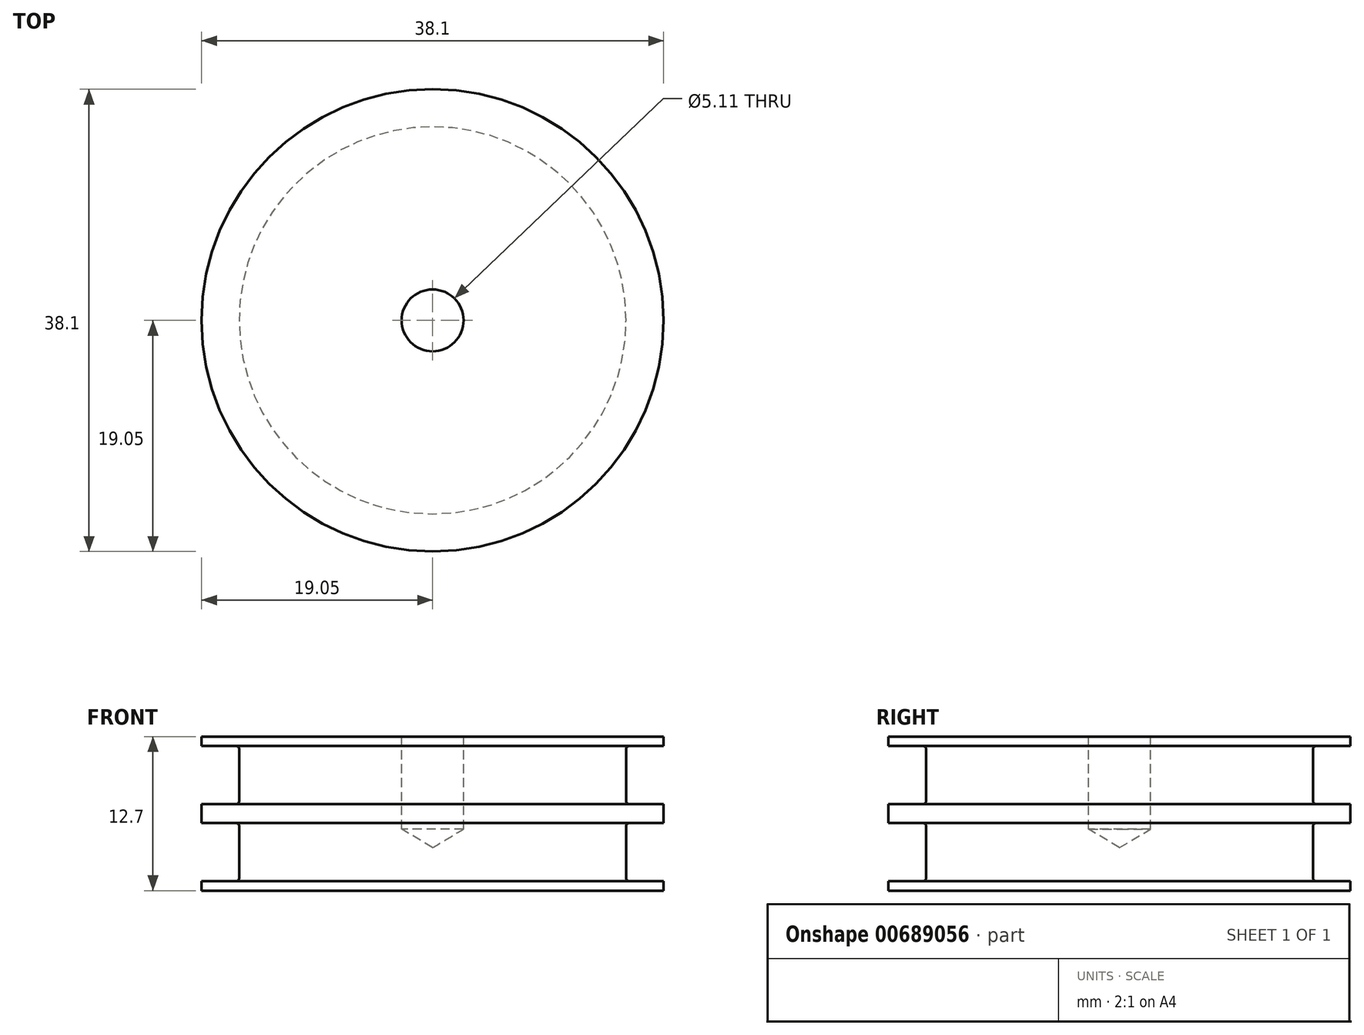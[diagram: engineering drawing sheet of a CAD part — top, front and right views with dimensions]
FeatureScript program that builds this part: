
annotation { "Feature Type Name" : "Feature", "Feature Type Description" : "" }
export const myFeature = defineFeature(function(context is Context, id is Id, definition is map)
    precondition{}
    {
        {
            var Q0;
            Q0=qCreatedBy(makeId("Front.planeOp"),FACE);
            var sketch = newSketch(context, id + "F0", { "sketchPlane" : qUnion([Q0])});
            skLineSegment(sketch, "E0.bottom", {"start": v(0, 12.7) * mm, "end": v(19.05, 12.7) * mm});
            skLineSegment(sketch, "E0.top", {"start": v(0, 0) * mm, "end": v(19.05, 0) * mm});
            skLineSegment(sketch, "E0.left", {"start": v(0, 12.7) * mm, "end": v(0, 0) * mm});
            skLineSegment(sketch, "E0.right", {"start": v(19.05, 12.7) * mm, "end": v(19.05, 11.91) * mm});
            skPoint(sketch, "E1", {"position": v(19.05, 6.35) * mm});
            skLineSegment(sketch, "E2", {"start": v(19.05, 6.35) * mm, "end": v(-2.1, 6.35) * mm, "construction": true});
            skPoint(sketch, "E3", {"position": v(19.05, 3.18) * mm});
            skLineSegment(sketch, "E4.top", {"start": v(19.05, 5.56) * mm, "end": v(16.2, 5.56) * mm});
            skLineSegment(sketch, "E4.right", {"start": v(15.95, 3.17) * mm, "end": v(15.95, 5.3) * mm});
            skLineSegment(sketch, "E5", {"start": v(15.95, 3.18) * mm, "end": v(3.84, 3.17) * mm, "construction": true});
            skLineSegment(sketch, "E6.MirrorCS", {"start": v(19.05, 0.79) * mm, "end": v(16.2, 0.79) * mm});
            skLineSegment(sketch, "E7.MirrorCS", {"start": v(15.95, 3.17) * mm, "end": v(15.95, 1.04) * mm});
            skPoint(sketch, "E8.visualSharp", {"position": v(15.95, 5.56) * mm});
            skArc(sketch, "E8.filletArc", {"start": v(16.2, 5.56) * mm, "mid": v(16.03, 5.49) * mm, "end": v(15.95, 5.3) * mm});
            skPoint(sketch, "E9.visualSharp", {"position": v(15.95, 0.79) * mm});
            skArc(sketch, "E9.filletArc", {"start": v(15.95, 1.04) * mm, "mid": v(16.03, 0.86) * mm, "end": v(16.2, 0.79) * mm});
            skLineSegment(sketch, "E10.MirrorCS", {"start": v(19.05, 7.14) * mm, "end": v(16.2, 7.14) * mm});
            skLineSegment(sketch, "E11.MirrorCS", {"start": v(15.95, 9.53) * mm, "end": v(15.95, 7.4) * mm});
            skLineSegment(sketch, "E12.MirrorCS", {"start": v(15.95, 9.53) * mm, "end": v(15.95, 11.66) * mm});
            skLineSegment(sketch, "E13.MirrorCS", {"start": v(19.05, 11.91) * mm, "end": v(16.2, 11.91) * mm});
            skLineSegment(sketch, "E14.trimOffspring", {"start": v(19.05, 7.14) * mm, "end": v(19.05, 5.56) * mm});
            skArc(sketch, "E15.MirrorCS", {"start": v(16.2, 7.14) * mm, "mid": v(16.03, 7.21) * mm, "end": v(15.95, 7.4) * mm});
            skArc(sketch, "E16.MirrorCS", {"start": v(15.95, 11.66) * mm, "mid": v(16.03, 11.84) * mm, "end": v(16.2, 11.91) * mm});
            skLineSegment(sketch, "E17.trimOffspring", {"start": v(19.05, 0.79) * mm, "end": v(19.05, 0) * mm});
            skSolve(sketch);
        }
        {
            var Q0;
            Q0=makeQuery(id+"F0.imprint","IMPRINT",FACE,{"disambiguationData":[TD([[makeQuery(id+"F0.imprint","IMPRINT",EDGE,{"derivedFrom":sQuery(id+"F0.wireOp",EDGE,"E0.bottom")}),-1.0]])]});
            var Q1;
            Q1=sQuery(id+"F0.wireOp",EDGE,"E0.left");
            revolve(context, id + "F1", {"entities" : qUnion([Q0]), "axis" : qUnion([Q1]), "revolveType" : RevolveType.FULL});
        }
        {
            var Q0;
            Q0=makeQuery(id+"F1.opRevolve","SWEPT_FACE",FACE,{"disambiguationData":[OSD([sQuery(id+"F0.wireOp",EDGE,"E0.bottom")])]});
            var sketch = newSketch(context, id + "F2", { "sketchPlane" : qUnion([Q0])});
            skPoint(sketch, "E18", {"position": v(0, 0) * mm});
            skSolve(sketch);
        }
        {
            var Q0;
            Q0=sQuery(id+"F2.wireOp",VERTEX,"E18");
            var Q1;
            Q1=makeQuery(id+"F1.opRevolve","SWEPT_BODY",BODY,{"disambiguationData":[OSD([sQuery(id+"F0.wireOp",EDGE,"E0.bottom"),sQuery(id+"F0.wireOp",EDGE,"E0.top"),sQuery(id+"F0.wireOp",EDGE,"E0.left"),sQuery(id+"F0.wireOp",EDGE,"E0.right"),sQuery(id+"F0.wireOp",EDGE,"E4.top"),sQuery(id+"F0.wireOp",EDGE,"E4.right"),sQuery(id+"F0.wireOp",EDGE,"E6.MirrorCS"),sQuery(id+"F0.wireOp",EDGE,"E7.MirrorCS"),sQuery(id+"F0.wireOp",EDGE,"E8.filletArc"),sQuery(id+"F0.wireOp",EDGE,"E9.filletArc"),sQuery(id+"F0.wireOp",EDGE,"E10.MirrorCS"),sQuery(id+"F0.wireOp",EDGE,"E11.MirrorCS"),sQuery(id+"F0.wireOp",EDGE,"E12.MirrorCS"),sQuery(id+"F0.wireOp",EDGE,"E13.MirrorCS"),sQuery(id+"F0.wireOp",EDGE,"E14.trimOffspring"),sQuery(id+"F0.wireOp",EDGE,"E15.MirrorCS"),sQuery(id+"F0.wireOp",EDGE,"E16.MirrorCS"),sQuery(id+"F0.wireOp",EDGE,"E17.trimOffspring")])]});
            hole(context, id + "F3", {"style" : HoleStyle.SIMPLE, "endStyle" : HoleEndStyle.BLIND, "standardTappedOrClearance" : lookupTablePath({ "standard" : "ANSI", "engagement" : "75%", "pitch" : "20 tpi", "size" : "1/4", "type" : "Tapped" }), "standardBlindInLast" : lookupTablePath({ "standard" : "ANSI", "engagement" : "75%", "pitch" : "20 tpi", "size" : "1/4", "type" : "Tapped" }), "holeDiameter" : 5.1 * mm, "majorDiameter" : 6.35 * mm, "showTappedDepth" : true, "holeDepth" : 7.62 * mm, "isTappedThrough" : true, "tappedDepth" : 6.35 * mm, "tapClearance" : 1, "startFromSketch" : true, "locations" : qUnion([Q0]), "scope" : qUnion([Q1])});
        }
    });
